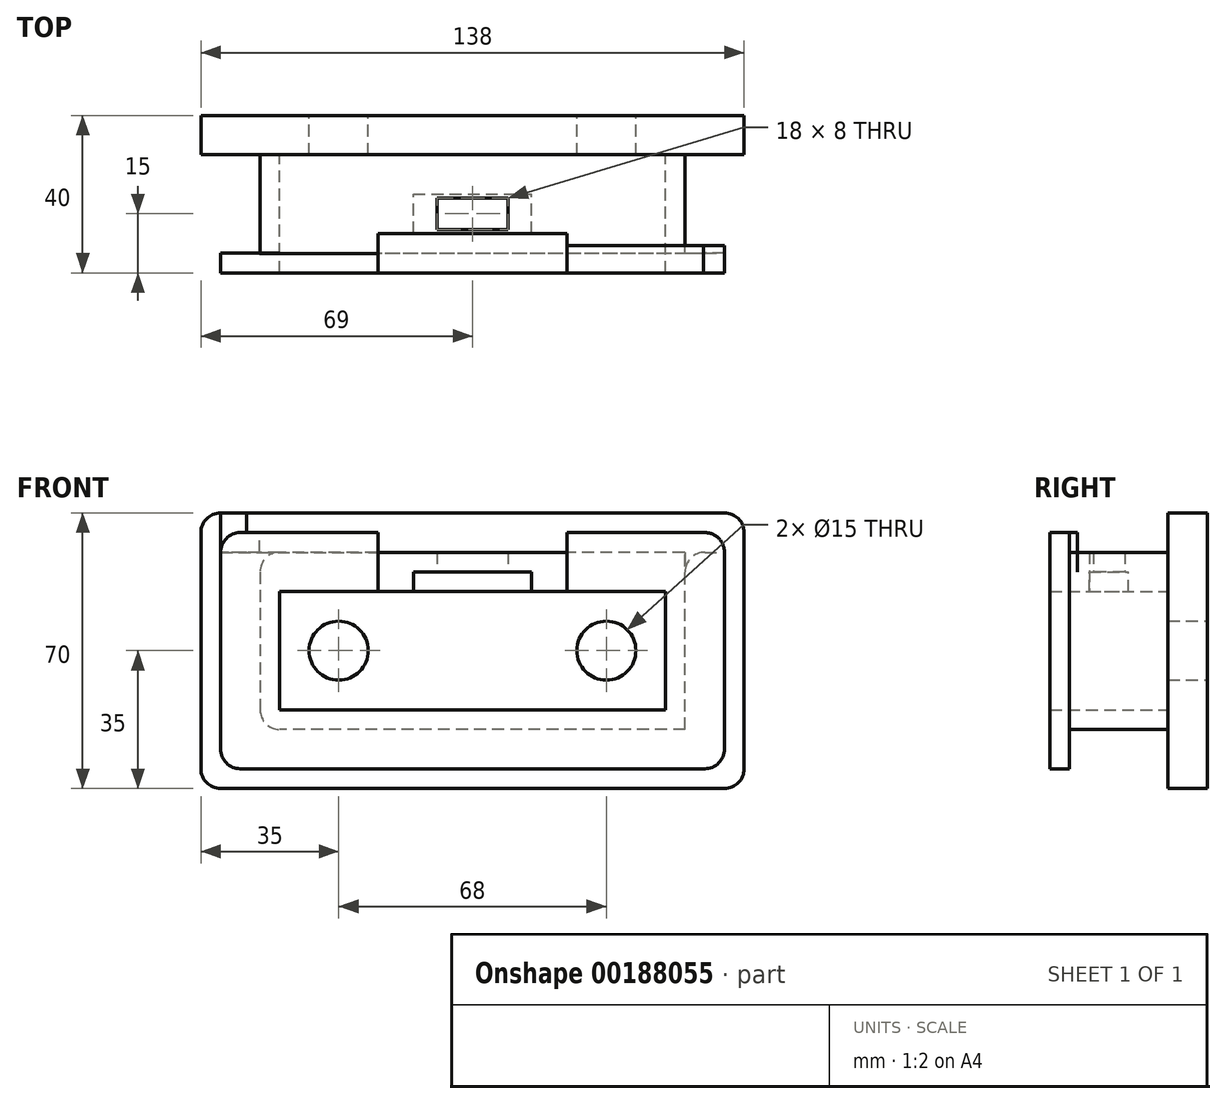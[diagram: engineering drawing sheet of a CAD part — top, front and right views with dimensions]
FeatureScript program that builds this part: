
annotation { "Feature Type Name" : "Feature", "Feature Type Description" : "" }
export const myFeature = defineFeature(function(context is Context, id is Id, definition is map)
    precondition{}
    {
        {
            var Q0;
            Q0=qCreatedBy(makeId("Front.planeOp"),FACE);
            var sketch = newSketch(context, id + "F0", { "sketchPlane" : qUnion([Q0])});
            skPoint(sketch, "E0", {"position": v(0, 0) * mm});
            skLineSegment(sketch, "E1.bottom", {"start": v(-64, 35) * mm, "end": v(64, 35) * mm});
            skLineSegment(sketch, "E1.top", {"start": v(-64, -35) * mm, "end": v(64, -35) * mm});
            skLineSegment(sketch, "E1.left", {"start": v(-69, 30) * mm, "end": v(-69, -30) * mm});
            skLineSegment(sketch, "E1.right", {"start": v(69, 30) * mm, "end": v(69, -30) * mm});
            skPoint(sketch, "E2.visualSharp", {"position": v(69, -35) * mm});
            skArc(sketch, "E2.filletArc", {"start": v(64, -35) * mm, "mid": v(67.54, -33.54) * mm, "end": v(69, -30) * mm});
            skPoint(sketch, "E3.visualSharp", {"position": v(-69, -35) * mm});
            skArc(sketch, "E3.filletArc", {"start": v(-69, -30) * mm, "mid": v(-67.54, -33.54) * mm, "end": v(-64, -35) * mm});
            skPoint(sketch, "E4.visualSharp", {"position": v(-69, 35) * mm});
            skArc(sketch, "E4.filletArc", {"start": v(-64, 35) * mm, "mid": v(-67.54, 33.54) * mm, "end": v(-69, 30) * mm});
            skPoint(sketch, "E5.visualSharp", {"position": v(69, 35) * mm});
            skArc(sketch, "E5.filletArc", {"start": v(69, 30) * mm, "mid": v(67.54, 33.54) * mm, "end": v(64, 35) * mm});
            skLineSegment(sketch, "E6", {"start": v(64, -25) * mm, "end": v(64, 25) * mm});
            skLineSegment(sketch, "E7", {"start": v(59, -30) * mm, "end": v(-59, -30) * mm});
            skLineSegment(sketch, "E8", {"start": v(-64, 25) * mm, "end": v(-64, -25) * mm});
            skArc(sketch, "E9.filletArc", {"start": v(-59, 30) * mm, "mid": v(-62.54, 28.54) * mm, "end": v(-64, 25) * mm});
            skArc(sketch, "E10.filletArc", {"start": v(59, -30) * mm, "mid": v(62.54, -28.54) * mm, "end": v(64, -25) * mm});
            skArc(sketch, "E11.filletArc", {"start": v(-64, -25) * mm, "mid": v(-62.54, -28.54) * mm, "end": v(-59, -30) * mm});
            skArc(sketch, "E12.filletArc", {"start": v(64, 25) * mm, "mid": v(62.43, 28.65) * mm, "end": v(58.7, 30) * mm});
            skLineSegment(sketch, "E13", {"start": v(-49, 15) * mm, "end": v(-15, 15) * mm});
            skLineSegment(sketch, "E14", {"start": v(-15, 15) * mm, "end": v(-15, 20) * mm});
            skLineSegment(sketch, "E15", {"start": v(-15, 20) * mm, "end": v(15, 20) * mm});
            skLineSegment(sketch, "E16", {"start": v(15, 20) * mm, "end": v(15, 15) * mm});
            skLineSegment(sketch, "E17", {"start": v(15, 15) * mm, "end": v(49, 15) * mm});
            skLineSegment(sketch, "E18", {"start": v(49, 15) * mm, "end": v(49, -15) * mm});
            skLineSegment(sketch, "E19", {"start": v(49, -15) * mm, "end": v(-49, -15) * mm});
            skLineSegment(sketch, "E20", {"start": v(-49, 15) * mm, "end": v(-49, -15) * mm});
            skLineSegment(sketch, "E21", {"start": v(58.7, 30) * mm, "end": v(24, 30) * mm});
            skLineSegment(sketch, "E22", {"start": v(24, 30) * mm, "end": v(24, 15) * mm});
            skLineSegment(sketch, "E23", {"start": v(24, 25) * mm, "end": v(-24, 25) * mm});
            skLineSegment(sketch, "E24", {"start": v(-24, 25) * mm, "end": v(-24, 15) * mm});
            skLineSegment(sketch, "E25", {"start": v(-59, 30) * mm, "end": v(-24, 30) * mm});
            skLineSegment(sketch, "E26", {"start": v(-24, 30) * mm, "end": v(-24, 15) * mm});
            skPoint(sketch, "E27", {"position": v(-34, 0) * mm});
            skPoint(sketch, "E28", {"position": v(34, 0) * mm});
            skCircle(sketch, "E29", {"center": v(-34, 0) * mm, "radius": 5.5 * mm});
            skCircle(sketch, "E30", {"center": v(34, 0) * mm, "radius": 5.5 * mm});
            skCircle(sketch, "E31", {"center": v(-34, 0) * mm, "radius": 7.5 * mm});
            skCircle(sketch, "E32", {"center": v(34, 0) * mm, "radius": 7.5 * mm});
            skLineSegment(sketch, "E33", {"start": v(-15, 15) * mm, "end": v(15, 15) * mm});
            skSolve(sketch);
        }
        {
            var Q0;
            Q0=makeQuery(id+"F0.imprint","IMPRINT",FACE,{"disambiguationData":[TD([[makeQuery(id+"F0.imprint","IMPRINT",EDGE,{"derivedFrom":sQuery(id+"F0.wireOp",EDGE,"E1.bottom")}),-1.0]])]});
            extrude(context, id + "F1", {"entities" : qUnion([Q0]), "depth" : 10 * mm});
        }
        {
            var Q0;
            Q0=makeQuery(id+"F0.imprint","IMPRINT",FACE,{"disambiguationData":[TD([[makeQuery(id+"F0.imprint","IMPRINT",EDGE,{"derivedFrom":sQuery(id+"F0.wireOp",EDGE,"E6")}),1.0]])]});
            extrude(context, id + "F2", {"entities" : qUnion([Q0]), "operationType" : NewBodyOperationType.ADD, "depth" : 40 * mm});
        }
        {
            var Q0;
            {var subQ1=sQuery(id+"F0.wireOp",EDGE,"E14");Q0=makeQuery(id+"F0.imprint","IMPRINT",FACE,{"disambiguationData":[TD([[makeQuery(id+"F0.imprint","IMPRINT",EDGE,{"derivedFrom":subQ1}),1.0]])]});}
            extrude(context, id + "F3", {"entities" : qUnion([Q0]), "operationType" : NewBodyOperationType.ADD, "depth" : 30 * mm});
        }
        {
            var Q0;
            {var subQ7=sQuery(id+"F0.wireOp",EDGE,"E14");Q0=makeQuery(id+"F0.imprint","IMPRINT",FACE,{"disambiguationData":[TD([[makeQuery(id+"F0.imprint","IMPRINT",EDGE,{"derivedFrom":subQ7}),-1.0]])]});}
            extrude(context, id + "F4", {"entities" : qUnion([Q0]), "operationType" : NewBodyOperationType.ADD, "depth" : 20 * mm});
        }
        {
            var Q0;
            {var subQ0=sQuery(id+"F0.wireOp",EDGE,"E18");Q0=makeQuery(id+"F0.imprint","IMPRINT",FACE,{"disambiguationData":[TD([[makeQuery(id+"F0.imprint","IMPRINT",EDGE,{"derivedFrom":subQ0}),-1.0]])]});}
            extrude(context, id + "F5", {"entities" : qUnion([Q0]), "operationType" : NewBodyOperationType.ADD, "depth" : 10 * mm});
        }
        {
            var Q0;
            Q0=makeQuery(id+"F2.opExtrude","SWEPT_FACE",FACE,{"disambiguationData":[OSD([sQuery(id+"F0.wireOp",EDGE,"E7")])]});
            var sketch = newSketch(context, id + "F6", { "sketchPlane" : qUnion([Q0])});
            skPoint(sketch, "E34", {"position": v(59, 10) * mm});
            skPoint(sketch, "E35", {"position": v(-59, 10) * mm});
            skLineSegment(sketch, "E36.bottom", {"start": v(-59, 35) * mm, "end": v(59, 35) * mm});
            skLineSegment(sketch, "E36.top", {"start": v(-59, 10) * mm, "end": v(59, 10) * mm});
            skLineSegment(sketch, "E36.left", {"start": v(-59, 35) * mm, "end": v(-59, 10) * mm});
            skLineSegment(sketch, "E36.right", {"start": v(59, 35) * mm, "end": v(59, 10) * mm});
            skPoint(sketch, "E37", {"position": v(59, 35) * mm});
            skPoint(sketch, "E38", {"position": v(-59, 35) * mm});
            skSolve(sketch);
        }
        {
            var Q0;
            Q0 = qSketchRegion(id + "F6", true);
            extrude(context, id + "F7", {"entities" : qUnion([Q0]), "operationType" : NewBodyOperationType.REMOVE, "oppositeDirection" : true, "depth" : 10 * mm});
        }
        {
            var Q0;
            Q0=makeQuery(id+"F7.boolean.opBoolean","COPY",FACE,{"derivedFrom":makeQuery(id+"F7.opExtrude","SWEPT_FACE",FACE,{"disambiguationData":[OSD([sQuery(id+"F6.wireOp",EDGE,"E36.left")])]})});
            var sketch = newSketch(context, id + "F8", { "sketchPlane" : qUnion([Q0])});
            skSolve(sketch);
        }
        {
            var Q0;
            Q0=makeQuery(id+"F2.opExtrude","SWEPT_FACE",FACE,{"disambiguationData":[OSD([sQuery(id+"F0.wireOp",EDGE,"E8")])]});
            var sketch = newSketch(context, id + "F9", { "sketchPlane" : qUnion([Q0])});
            skPoint(sketch, "E39", {"position": v(10, 25) * mm});
            skPoint(sketch, "E40", {"position": v(10, -25) * mm});
            skLineSegment(sketch, "E41.bottom", {"start": v(35, 25) * mm, "end": v(10, 25) * mm});
            skLineSegment(sketch, "E41.top", {"start": v(35, -25) * mm, "end": v(10, -25) * mm});
            skLineSegment(sketch, "E41.left", {"start": v(35, 25) * mm, "end": v(35, -25) * mm});
            skLineSegment(sketch, "E41.right", {"start": v(10, 25) * mm, "end": v(10, -25) * mm});
            skSolve(sketch);
        }
        {
            var Q0;
            {var subQ0=sQuery(id+"F6.wireOp",EDGE,"E36.left");Q0=makeQuery(id+"F8.imprint","IMPRINT",FACE,{"disambiguationData":[TD([[makeQuery(id+"F8.imprint","IMPRINT",EDGE,{"derivedFrom":makeQuery(id+"F7.boolean.opBoolean","COPY",EDGE,{"derivedFrom":makeQuery(id+"F7.opExtrude","CAP_EDGE",EDGE,{"disambiguationData":[OSD([subQ0])],"isStart":false})})}),-1.0]])]});}
            extrude(context, id + "F10", {"entities" : qUnion([Q0]), "operationType" : NewBodyOperationType.REMOVE, "oppositeDirection" : true, "depth" : 25 * mm});
        }
        {
            var Q0;
            Q0=makeQuery(id+"F9.imprint","IMPRINT",FACE,{"disambiguationData":[TD([[makeQuery(id+"F9.imprint","IMPRINT",EDGE,{"derivedFrom":sQuery(id+"F9.wireOp",EDGE,"E41.bottom")}),1.0]])]});
            extrude(context, id + "F11", {"entities" : qUnion([Q0]), "operationType" : NewBodyOperationType.REMOVE, "oppositeDirection" : true, "depth" : 10 * mm});
        }
        {
            var Q0;
            Q0=makeQuery(id+"F11.boolean.opBoolean","COPY",FACE,{"derivedFrom":makeQuery(id+"F11.opExtrude","SWEPT_FACE",FACE,{"disambiguationData":[OSD([sQuery(id+"F9.wireOp",EDGE,"E41.bottom")])]})});
            var sketch = newSketch(context, id + "F12", { "sketchPlane" : qUnion([Q0])});
            skSolve(sketch);
        }
        {
            var Q0;
            {var subQ0=sQuery(id+"F9.wireOp",EDGE,"E41.bottom");Q0=makeQuery(id+"F12.imprint","IMPRINT",FACE,{"disambiguationData":[TD([[makeQuery(id+"F12.imprint","IMPRINT",EDGE,{"derivedFrom":makeQuery(id+"F11.boolean.opBoolean","COPY",EDGE,{"derivedFrom":makeQuery(id+"F11.opExtrude","CAP_EDGE",EDGE,{"disambiguationData":[OSD([subQ0])],"isStart":false})})}),-1.0]])]});}
            var sketch = newSketch(context, id + "F13", { "sketchPlane" : qUnion([Q0])});
            skPoint(sketch, "E42", {"position": v(-54.03, 10.04) * mm});
            skPoint(sketch, "E43", {"position": v(-64.06, 9.9) * mm});
            skPoint(sketch, "E44", {"position": v(-64.18, 35) * mm});
            skPoint(sketch, "E45", {"position": v(-54.04, 35.07) * mm});
            skLineSegment(sketch, "E46", {"start": v(-64.18, 35) * mm, "end": v(-54.04, 35.07) * mm});
            skLineSegment(sketch, "E47", {"start": v(-54.03, 10.04) * mm, "end": v(-64.06, 9.9) * mm});
            skLineSegment(sketch, "E48", {"start": v(-64.18, 35) * mm, "end": v(-64.06, 9.9) * mm});
            skLineSegment(sketch, "E49", {"start": v(-54.04, 35.07) * mm, "end": v(-54.03, 10.04) * mm});
            skSolve(sketch);
        }
        {
            var Q0;
            Q0 = qSketchRegion(id + "F13", true);
            extrude(context, id + "F14", {"entities" : qUnion([Q0]), "operationType" : NewBodyOperationType.REMOVE, "oppositeDirection" : true, "depth" : 25 * mm});
        }
        {
            var Q0;
            Q0=makeQuery(id+"F7.boolean.opBoolean","COPY",FACE,{"derivedFrom":makeQuery(id+"F7.opExtrude","SWEPT_FACE",FACE,{"disambiguationData":[OSD([sQuery(id+"F6.wireOp",EDGE,"E36.right")])]})});
            var sketch = newSketch(context, id + "F15", { "sketchPlane" : qUnion([Q0])});
            skLineSegment(sketch, "E50.bottom", {"start": v(35, -30) * mm, "end": v(35, -30) * mm});
            skLineSegment(sketch, "E50.top", {"start": v(35, -20) * mm, "end": v(35, -20) * mm});
            skLineSegment(sketch, "E50.left", {"start": v(35, -30) * mm, "end": v(35, -20) * mm});
            skLineSegment(sketch, "E50.right", {"start": v(35, -30) * mm, "end": v(35, -20) * mm});
            skLineSegment(sketch, "E51", {"start": v(35, -30) * mm, "end": v(10, -30) * mm});
            skLineSegment(sketch, "E52", {"start": v(10, -30) * mm, "end": v(10, -20) * mm});
            skLineSegment(sketch, "E53", {"start": v(10, -20) * mm, "end": v(35, -20) * mm});
            skSolve(sketch);
        }
        {
            var Q0;
            Q0 = qSketchRegion(id + "F15", true);
            extrude(context, id + "F16", {"entities" : qUnion([Q0]), "operationType" : NewBodyOperationType.REMOVE, "oppositeDirection" : true, "depth" : 25 * mm});
        }
        {
            var Q0;
            Q0=makeQuery(id+"F2.opExtrude","SWEPT_FACE",FACE,{"disambiguationData":[OSD([sQuery(id+"F0.wireOp",EDGE,"E6")])]});
            var sketch = newSketch(context, id + "F17", { "sketchPlane" : qUnion([Q0])});
            skLineSegment(sketch, "E54", {"start": v(-35, -20) * mm, "end": v(-35, 25) * mm});
            skLineSegment(sketch, "E55", {"start": v(-35, 25) * mm, "end": v(-10, 25) * mm});
            skLineSegment(sketch, "E56", {"start": v(-10, 25) * mm, "end": v(-10, -20) * mm});
            skLineSegment(sketch, "E57", {"start": v(-10, -20) * mm, "end": v(-35, -20) * mm});
            skSolve(sketch);
        }
        {
            var Q0;
            Q0 = qSketchRegion(id + "F17", true);
            extrude(context, id + "F18", {"entities" : qUnion([Q0]), "operationType" : NewBodyOperationType.REMOVE, "oppositeDirection" : true, "depth" : 10 * mm});
        }
        {
            var Q0;
            Q0=makeQuery(id+"F18.boolean.opBoolean","COPY",FACE,{"derivedFrom":makeQuery(id+"F18.opExtrude","SWEPT_FACE",FACE,{"disambiguationData":[OSD([sQuery(id+"F17.wireOp",EDGE,"E55")])]})});
            var sketch = newSketch(context, id + "F19", { "sketchPlane" : qUnion([Q0])});
            skSolve(sketch);
        }
        {
            var Q0;
            {var subQ0=sQuery(id+"F17.wireOp",EDGE,"E55");Q0=makeQuery(id+"F19.imprint","IMPRINT",FACE,{"disambiguationData":[TD([[makeQuery(id+"F19.imprint","IMPRINT",EDGE,{"derivedFrom":makeQuery(id+"F18.boolean.opBoolean","COPY",EDGE,{"derivedFrom":makeQuery(id+"F18.opExtrude","CAP_EDGE",EDGE,{"disambiguationData":[OSD([subQ0])],"isStart":false})})}),1.0]])]});}
            var sketch = newSketch(context, id + "F20", { "sketchPlane" : qUnion([Q0])});
            skLineSegment(sketch, "E58", {"start": v(64.15, 10) * mm, "end": v(53.85, 10) * mm});
            skLineSegment(sketch, "E59", {"start": v(53.85, 10) * mm, "end": v(53.85, 33.02) * mm});
            skLineSegment(sketch, "E60", {"start": v(53.85, 33.02) * mm, "end": v(64.15, 33.02) * mm});
            skLineSegment(sketch, "E61", {"start": v(64.15, 33.02) * mm, "end": v(64.15, 10) * mm});
            skSolve(sketch);
        }
        {
            var Q0;
            Q0 = qSketchRegion(id + "F20", true);
            extrude(context, id + "F21", {"entities" : qUnion([Q0]), "operationType" : NewBodyOperationType.REMOVE, "oppositeDirection" : true, "depth" : 25 * mm});
        }
        {
            var Q0;
            Q0 = qSketchRegion(id + "F20", true);
            extrude(context, id + "F22", {"entities" : qUnion([Q0]), "operationType" : NewBodyOperationType.REMOVE, "oppositeDirection" : true, "depth" : 10 * mm});
        }
        {
            var Q0;
            Q0=makeQuery(id+"F2.opExtrude","SWEPT_FACE",FACE,{"disambiguationData":[OSD([sQuery(id+"F0.wireOp",EDGE,"E21")])]});
            var sketch = newSketch(context, id + "F23", { "sketchPlane" : qUnion([Q0])});
            skLineSegment(sketch, "E62.bottom", {"start": v(53.85, -33.02) * mm, "end": v(24, -33.02) * mm});
            skLineSegment(sketch, "E62.top", {"start": v(53.85, -10) * mm, "end": v(24, -10) * mm});
            skLineSegment(sketch, "E62.left", {"start": v(53.85, -33.02) * mm, "end": v(53.85, -10) * mm});
            skLineSegment(sketch, "E62.right", {"start": v(24, -33.02) * mm, "end": v(24, -10) * mm});
            skSolve(sketch);
        }
        {
            var Q0;
            Q0 = qSketchRegion(id + "F23", true);
            extrude(context, id + "F24", {"entities" : qUnion([Q0]), "operationType" : NewBodyOperationType.REMOVE, "oppositeDirection" : true, "depth" : 5 * mm});
        }
        {
            var Q0;
            Q0=makeQuery(id+"F2.opExtrude","SWEPT_FACE",FACE,{"disambiguationData":[OSD([sQuery(id+"F0.wireOp",EDGE,"E25")])]});
            var sketch = newSketch(context, id + "F25", { "sketchPlane" : qUnion([Q0])});
            skLineSegment(sketch, "E63.bottom", {"start": v(-54.04, -35.07) * mm, "end": v(-24, -35.07) * mm});
            skLineSegment(sketch, "E63.top", {"start": v(-54.04, -10) * mm, "end": v(-24, -10) * mm});
            skLineSegment(sketch, "E63.left", {"start": v(-54.04, -35.07) * mm, "end": v(-54.04, -10) * mm});
            skLineSegment(sketch, "E63.right", {"start": v(-24, -35.07) * mm, "end": v(-24, -10) * mm});
            skSolve(sketch);
        }
        {
            var Q0;
            Q0 = qSketchRegion(id + "F25", true);
            extrude(context, id + "F26", {"entities" : qUnion([Q0]), "operationType" : NewBodyOperationType.REMOVE, "oppositeDirection" : true, "depth" : 5 * mm});
        }
        {
            var Q0;
            Q0=makeQuery(id+"F3.opExtrude","SWEPT_FACE",FACE,{"disambiguationData":[OSD([sQuery(id+"F0.wireOp",EDGE,"E15")])]});
            var sketch = newSketch(context, id + "F27", { "sketchPlane" : qUnion([Q0])});
            skLineSegment(sketch, "E64.bottom", {"start": v(9, 21) * mm, "end": v(-9, 21) * mm});
            skLineSegment(sketch, "E64.top", {"start": v(9, 29) * mm, "end": v(-9, 29) * mm});
            skLineSegment(sketch, "E64.left", {"start": v(9, 21) * mm, "end": v(9, 29) * mm});
            skLineSegment(sketch, "E64.right", {"start": v(-9, 21) * mm, "end": v(-9, 29) * mm});
            skSolve(sketch);
        }
        {
            var Q0;
            Q0 = qSketchRegion(id + "F27", true);
            extrude(context, id + "F28", {"entities" : qUnion([Q0]), "operationType" : NewBodyOperationType.REMOVE, "oppositeDirection" : true, "depth" : 25 * mm});
        }
        {
            var Q0;
            {var subQ2=sQuery(id+"F17.wireOp",EDGE,"E55");var subQ4=sQuery(id+"F6.wireOp",EDGE,"E36.top");Q0=makeQuery(id+"F21.boolean.opBoolean","SPLIT",EDGE,{"disambiguationData":[TD([makeQuery(id+"F7.opExtrude","SWEPT_FACE",FACE,{"disambiguationData":[OSD([subQ4])]})])],"derivedFrom":makeQuery(id+"F18.boolean.opBoolean","COPY",EDGE,{"derivedFrom":makeQuery(id+"F18.opExtrude","CAP_EDGE",EDGE,{"disambiguationData":[OSD([subQ2])],"isStart":false})})});}
            var Q1;
            Q1=makeQuery(id+"F18.boolean.opBoolean","COPY",EDGE,{"derivedFrom":makeQuery(id+"F18.opExtrude","CAP_EDGE",EDGE,{"disambiguationData":[OSD([sQuery(id+"F17.wireOp",EDGE,"E57")])],"isStart":false})});
            fillet(context, id + "F29", {"entities" : qUnion([Q0, Q1]), "radius" : 5 * mm, "tangentPropagation" : true, "allowEdgeOverflow" : false});
        }
        {
            var Q0;
            {var subQ0=sQuery(id+"F6.wireOp",EDGE,"E36.left");Q0=makeQuery(id+"F11.boolean.opBoolean","INTERSECT",EDGE,{"derivedFrom":[makeQuery(id+"F10.boolean.opBoolean","MERGE",FACE,{"derivedFrom":[makeQuery(id+"F7.boolean.opBoolean","COPY",FACE,{"derivedFrom":makeQuery(id+"F7.opExtrude","CAP_FACE",FACE,{"disambiguationData":[OSD([sQuery(id+"F6.wireOp",EDGE,"E36.bottom"),sQuery(id+"F6.wireOp",EDGE,"E36.top"),subQ0,sQuery(id+"F6.wireOp",EDGE,"E36.right")])],"isStart":false})}),makeQuery(id+"F10.opExtrude","SWEPT_FACE",FACE,{"disambiguationData":[OSD([subQ0])]})]}),makeQuery(id+"F11.opExtrude","CAP_FACE",FACE,{"disambiguationData":[OSD([sQuery(id+"F9.wireOp",EDGE,"E41.bottom"),sQuery(id+"F9.wireOp",EDGE,"E41.top"),sQuery(id+"F9.wireOp",EDGE,"E41.left"),sQuery(id+"F9.wireOp",EDGE,"E41.right")])],"isStart":false})]});}
            var Q1;
            Q1=makeQuery(id+"F11.boolean.opBoolean","COPY",EDGE,{"derivedFrom":makeQuery(id+"F11.opExtrude","CAP_EDGE",EDGE,{"disambiguationData":[OSD([sQuery(id+"F9.wireOp",EDGE,"E41.bottom")])],"isStart":false})});
            fillet(context, id + "F30", {"entities" : qUnion([Q0, Q1]), "radius" : 5 * mm, "tangentPropagation" : true, "allowEdgeOverflow" : false});
        }
    });
